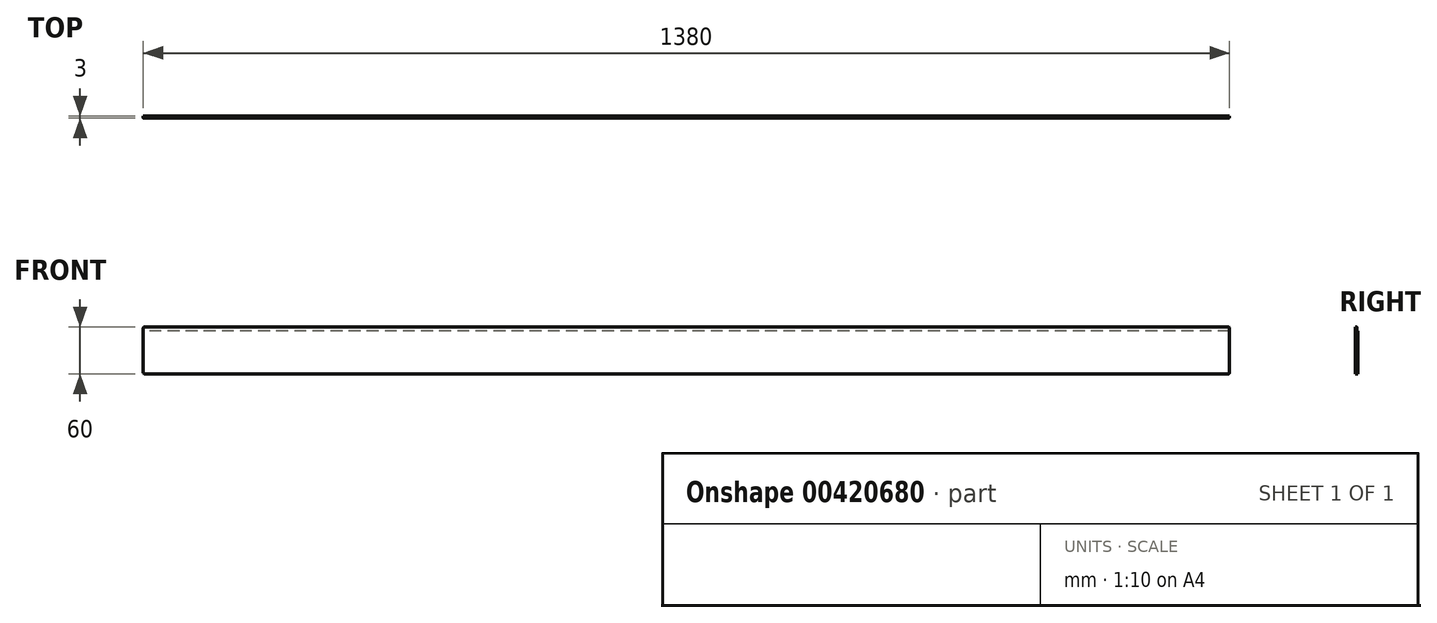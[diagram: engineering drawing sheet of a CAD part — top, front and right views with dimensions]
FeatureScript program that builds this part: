
annotation { "Feature Type Name" : "Feature", "Feature Type Description" : "" }
export const myFeature = defineFeature(function(context is Context, id is Id, definition is map)
    precondition{}
    {
        {
            var Q0;
            Q0=qCreatedBy(makeId("Front.planeOp"),FACE);
            var sketch = newSketch(context, id + "F0", { "sketchPlane" : qUnion([Q0])});
            skLineSegment(sketch, "E0.bottom", {"start": v(690, -30) * mm, "end": v(-690, -30) * mm});
            skLineSegment(sketch, "E0.top", {"start": v(690, 30) * mm, "end": v(-690, 30) * mm});
            skLineSegment(sketch, "E0.left", {"start": v(690, -30) * mm, "end": v(690, 30) * mm});
            skLineSegment(sketch, "E0.right", {"start": v(-690, -30) * mm, "end": v(-690, 30) * mm});
            skPoint(sketch, "E0.middle", {"position": v(0, 0) * mm});
            skSolve(sketch);
        }
        {
            var Q0;
            Q0=qSketchRegion(id+"F0",true);
            extrude(context, id + "F1", {"entities" : qUnion([Q0]), "depth" : 3 * mm});
        }
        {
            var Q0;
            Q0=makeQuery(id+"F1.opExtrude","CAP_FACE",FACE,{"disambiguationData":[OSD([sQuery(id+"F0.wireOp",EDGE,"E0.bottom"),sQuery(id+"F0.wireOp",EDGE,"E0.top"),sQuery(id+"F0.wireOp",EDGE,"E0.left"),sQuery(id+"F0.wireOp",EDGE,"E0.right")])],"isStart":true});
            var sketch = newSketch(context, id + "F2", { "sketchPlane" : qUnion([Q0])});
            skLineSegment(sketch, "E1", {"start": v(-690, 30) * mm, "end": v(-690, 25) * mm});
            skLineSegment(sketch, "E2", {"start": v(-690, 25) * mm, "end": v(690, 25) * mm});
            skPoint(sketch, "E2.endSnap0", {"position": v(690, 0) * mm});
            skLineSegment(sketch, "E3", {"start": v(690, 25) * mm, "end": v(690, 30) * mm});
            skLineSegment(sketch, "E4", {"start": v(690, 30) * mm, "end": v(-690, 30) * mm});
            skSolve(sketch);
        }
        {
            var Q0;
            Q0=qSketchRegion(id+"F2",true);
            extrude(context, id + "F3", {"entities" : qUnion([Q0]), "operationType" : NewBodyOperationType.REMOVE, "oppositeDirection" : true, "depth" : 1.5 * mm});
        }
        {
            var Q0;
            Q0=makeQuery(id+"F1.opExtrude","SWEPT_EDGE",EDGE,{"disambiguationData":[OSD([sQuery(id+"F0.wireOp",EDGE,"E0.top"),sQuery(id+"F0.wireOp",EDGE,"E0.left")])]});
            var Q1;
            Q1=makeQuery(id+"F1.opExtrude","SWEPT_EDGE",EDGE,{"disambiguationData":[OSD([sQuery(id+"F0.wireOp",EDGE,"E0.bottom"),sQuery(id+"F0.wireOp",EDGE,"E0.left")])]});
            var Q2;
            Q2=makeQuery(id+"F1.opExtrude","SWEPT_EDGE",EDGE,{"disambiguationData":[OSD([sQuery(id+"F0.wireOp",EDGE,"E0.top"),sQuery(id+"F0.wireOp",EDGE,"E0.right")])]});
            var Q3;
            Q3=makeQuery(id+"F1.opExtrude","SWEPT_EDGE",EDGE,{"disambiguationData":[OSD([sQuery(id+"F0.wireOp",EDGE,"E0.bottom"),sQuery(id+"F0.wireOp",EDGE,"E0.right")])]});
            fillet(context, id + "F4", {"entities" : qUnion([Q0, Q1, Q2, Q3]), "radius" : 2 * mm, "tangentPropagation" : true, "allowEdgeOverflow" : false});
        }
    });
